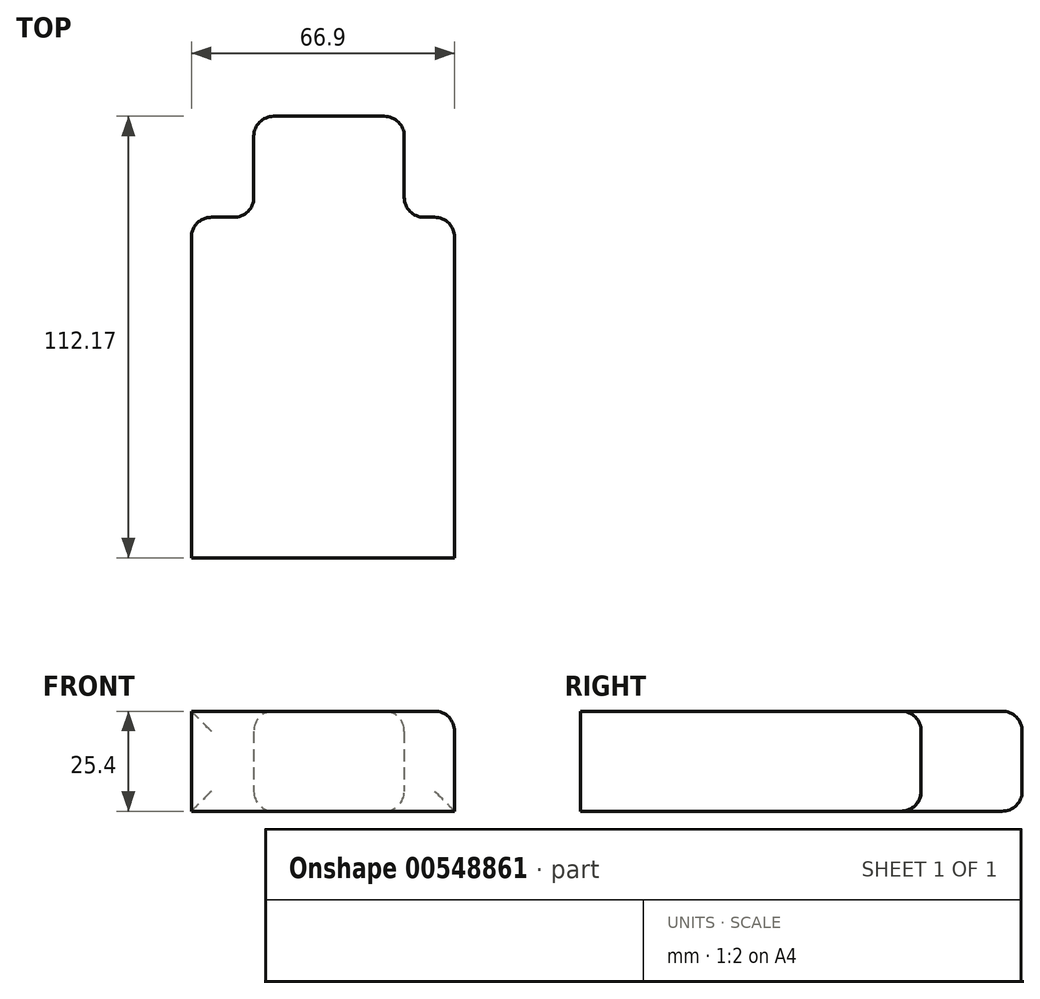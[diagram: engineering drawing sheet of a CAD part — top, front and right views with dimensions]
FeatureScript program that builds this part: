
annotation { "Feature Type Name" : "Feature", "Feature Type Description" : "" }
export const myFeature = defineFeature(function(context is Context, id is Id, definition is map)
    precondition{}
    {
        {
            var Q0;
            Q0=qCreatedBy(makeId("Top.planeOp"),FACE);
            var sketch = newSketch(context, id + "F0", { "sketchPlane" : qUnion([Q0])});
            skLineSegment(sketch, "E0.bottom", {"start": v(-33, 27) * mm, "end": v(-17.13, 27) * mm});
            skLineSegment(sketch, "E0.top", {"start": v(-33, -59.5) * mm, "end": v(33.9, -59.5) * mm});
            skLineSegment(sketch, "E0.left", {"start": v(-33, 27) * mm, "end": v(-33, -59.5) * mm});
            skLineSegment(sketch, "E0.right", {"start": v(33.9, 27) * mm, "end": v(33.9, -59.5) * mm});
            skLineSegment(sketch, "E1.bottom", {"start": v(-17.13, 52.66) * mm, "end": v(21.1, 52.66) * mm});
            skLineSegment(sketch, "E1.left", {"start": v(-17.13, 52.66) * mm, "end": v(-17.13, 27) * mm});
            skLineSegment(sketch, "E1.right", {"start": v(21.1, 52.66) * mm, "end": v(21.1, 27) * mm});
            skLineSegment(sketch, "E2.trimOffspring", {"start": v(21.1, 27) * mm, "end": v(33.9, 27) * mm});
            skPoint(sketch, "E3.orphan", {"position": v(21.1, 0) * mm});
            skSolve(sketch);
        }
        {
            var Q0;
            Q0=makeQuery(id+"F0.imprint","IMPRINT",FACE,{"disambiguationData":[TD([[makeQuery(id+"F0.imprint","IMPRINT",EDGE,{"derivedFrom":sQuery(id+"F0.wireOp",EDGE,"E0.bottom")}),-1.0]])]});
            extrude(context, id + "F1", {"entities" : qUnion([Q0]), "depth" : 25.4 * mm, "offsetDistance" : 25.4 * mm});
        }
        {
            var Q0;
            Q0=makeQuery(id+"F1.opExtrude","CAP_EDGE",EDGE,{"disambiguationData":[OSD([sQuery(id+"F0.wireOp",EDGE,"E1.right")])],"isStart":false});
            var Q1;
            Q1=makeQuery(id+"F1.opExtrude","CAP_EDGE",EDGE,{"disambiguationData":[OSD([sQuery(id+"F0.wireOp",EDGE,"E1.right")])],"isStart":true});
            var Q2;
            Q2=makeQuery(id+"F1.opExtrude","CAP_EDGE",EDGE,{"disambiguationData":[OSD([sQuery(id+"F0.wireOp",EDGE,"E0.bottom")])],"isStart":true});
            var Q3;
            Q3=makeQuery(id+"F1.opExtrude","CAP_EDGE",EDGE,{"disambiguationData":[OSD([sQuery(id+"F0.wireOp",EDGE,"E1.left")])],"isStart":true});
            var Q4;
            Q4=makeQuery(id+"F1.opExtrude","CAP_EDGE",EDGE,{"disambiguationData":[OSD([sQuery(id+"F0.wireOp",EDGE,"E2.trimOffspring")])],"isStart":true});
            var Q5;
            Q5=makeQuery(id+"F1.opExtrude","CAP_EDGE",EDGE,{"disambiguationData":[OSD([sQuery(id+"F0.wireOp",EDGE,"E2.trimOffspring")])],"isStart":false});
            var Q6;
            Q6=makeQuery(id+"F1.opExtrude","CAP_EDGE",EDGE,{"disambiguationData":[OSD([sQuery(id+"F0.wireOp",EDGE,"E1.left")])],"isStart":false});
            var Q7;
            Q7=makeQuery(id+"F1.opExtrude","CAP_EDGE",EDGE,{"disambiguationData":[OSD([sQuery(id+"F0.wireOp",EDGE,"E0.bottom")])],"isStart":false});
            var Q8;
            Q8=makeQuery(id+"F1.opExtrude","SWEPT_EDGE",EDGE,{"disambiguationData":[OSD([sQuery(id+"F0.wireOp",EDGE,"E0.bottom"),sQuery(id+"F0.wireOp",EDGE,"E1.left")])]});
            var Q9;
            Q9=makeQuery(id+"F1.opExtrude","SWEPT_EDGE",EDGE,{"disambiguationData":[OSD([sQuery(id+"F0.wireOp",EDGE,"E0.bottom"),sQuery(id+"F0.wireOp",EDGE,"E0.left")])]});
            var Q10;
            Q10=makeQuery(id+"F1.opExtrude","SWEPT_EDGE",EDGE,{"disambiguationData":[OSD([sQuery(id+"F0.wireOp",EDGE,"E1.bottom"),sQuery(id+"F0.wireOp",EDGE,"E1.left")])]});
            var Q11;
            Q11=makeQuery(id+"F1.opExtrude","CAP_EDGE",EDGE,{"disambiguationData":[OSD([sQuery(id+"F0.wireOp",EDGE,"E1.bottom")])],"isStart":false});
            var Q12;
            Q12=makeQuery(id+"F1.opExtrude","CAP_EDGE",EDGE,{"disambiguationData":[OSD([sQuery(id+"F0.wireOp",EDGE,"E1.bottom")])],"isStart":true});
            var Q13;
            Q13=makeQuery(id+"F1.opExtrude","SWEPT_EDGE",EDGE,{"disambiguationData":[OSD([sQuery(id+"F0.wireOp",EDGE,"E1.right"),sQuery(id+"F0.wireOp",EDGE,"E2.trimOffspring")])]});
            var Q14;
            Q14=makeQuery(id+"F1.opExtrude","SWEPT_EDGE",EDGE,{"disambiguationData":[OSD([sQuery(id+"F0.wireOp",EDGE,"E1.bottom"),sQuery(id+"F0.wireOp",EDGE,"E1.right")])]});
            var Q15;
            Q15=makeQuery(id+"F1.opExtrude","CAP_EDGE",EDGE,{"disambiguationData":[OSD([sQuery(id+"F0.wireOp",EDGE,"E0.right")])],"isStart":false});
            var Q16;
            Q16=makeQuery(id+"F1.opExtrude","SWEPT_EDGE",EDGE,{"disambiguationData":[OSD([sQuery(id+"F0.wireOp",EDGE,"E0.right"),sQuery(id+"F0.wireOp",EDGE,"E2.trimOffspring")])]});
            fillet(context, id + "F2", {"entities" : qUnion([Q0, Q1, Q2, Q3, Q4, Q5, Q6, Q7, Q8, Q9, Q10, Q11, Q12, Q13, Q14, Q15, Q16]), "radius" : 5.08 * mm, "tangentPropagation" : true, "allowEdgeOverflow" : false});
        }
    });
